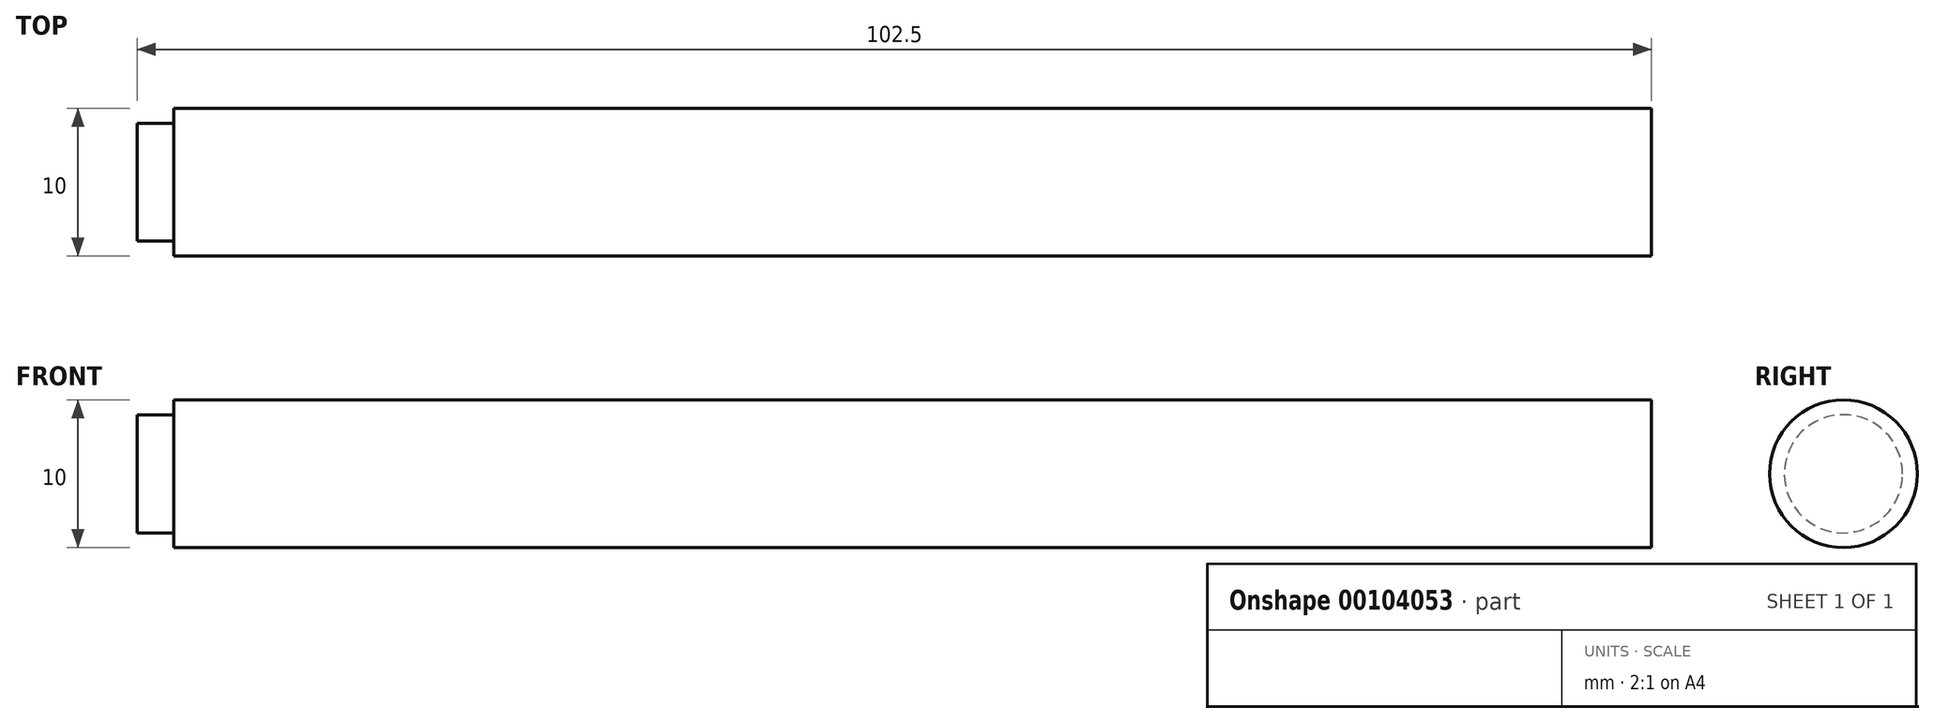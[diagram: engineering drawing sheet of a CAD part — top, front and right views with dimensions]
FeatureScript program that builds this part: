
annotation { "Feature Type Name" : "Feature", "Feature Type Description" : "" }
export const myFeature = defineFeature(function(context is Context, id is Id, definition is map)
    precondition{}
    {
        {
            var Q0;
            Q0=qCreatedBy(makeId("Right.planeOp"),FACE);
            var sketch = newSketch(context, id + "F0", { "sketchPlane" : qUnion([Q0])});
            skCircle(sketch, "E0", {"center": v(0, 0) * mm, "radius": 5 * mm});
            skSolve(sketch);
        }
        {
            var Q0;
            Q0 = qSketchRegion(id + "F0", true);
            extrude(context, id + "F1", {"entities" : qUnion([Q0]), "depth" : 100 * mm});
        }
        {
            var Q0;
            Q0=qCreatedBy(makeId("Right.planeOp"),FACE);
            var sketch = newSketch(context, id + "F2", { "sketchPlane" : qUnion([Q0])});
            skCircle(sketch, "E1", {"center": v(0, 0) * mm, "radius": 4 * mm});
            skSolve(sketch);
        }
        {
            var Q0;
            Q0 = qSketchRegion(id + "F2", true);
            extrude(context, id + "F3", {"entities" : qUnion([Q0]), "operationType" : NewBodyOperationType.ADD, "oppositeDirection" : true, "depth" : 2.5 * mm});
        }
    });
